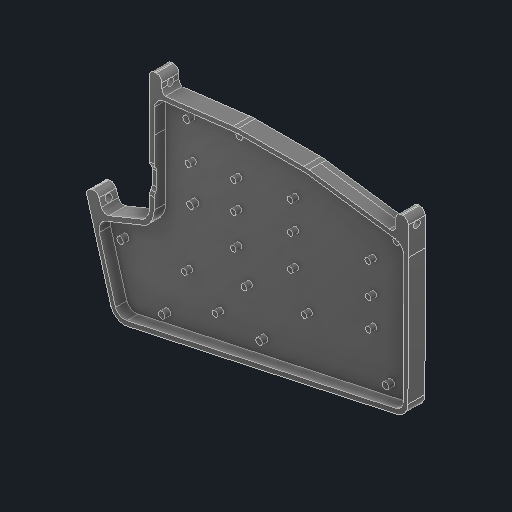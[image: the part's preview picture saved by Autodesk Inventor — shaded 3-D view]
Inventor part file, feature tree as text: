
AUTODESK INVENTOR PART (.ipt)
format: ipt  version: 2024.3 (Build 283343000, 343)  size: 355,328 bytes
history: native  units: in
note: dims shown in document units (in); Inventor stores cm internally (conversion verified against a paired STEP export)
features: other x3, sketch x3
ambient origin geometry x8: Origin, YZ Plane, XZ Plane, XY Plane, X Axis, Y Axis, Z Axis, Center Point
bodies: Solid1 (feature_tree)
feature tree (6):
  other  "Case Bottom.ipt"
  other  "Solid1::Case Bottom.ipt"
  other  "TaggingFeature1"
  sketch  "Sketch1"  dims[d0=0.3937in]
  sketch  "Sketch2"
  sketch  "Sketch3"
